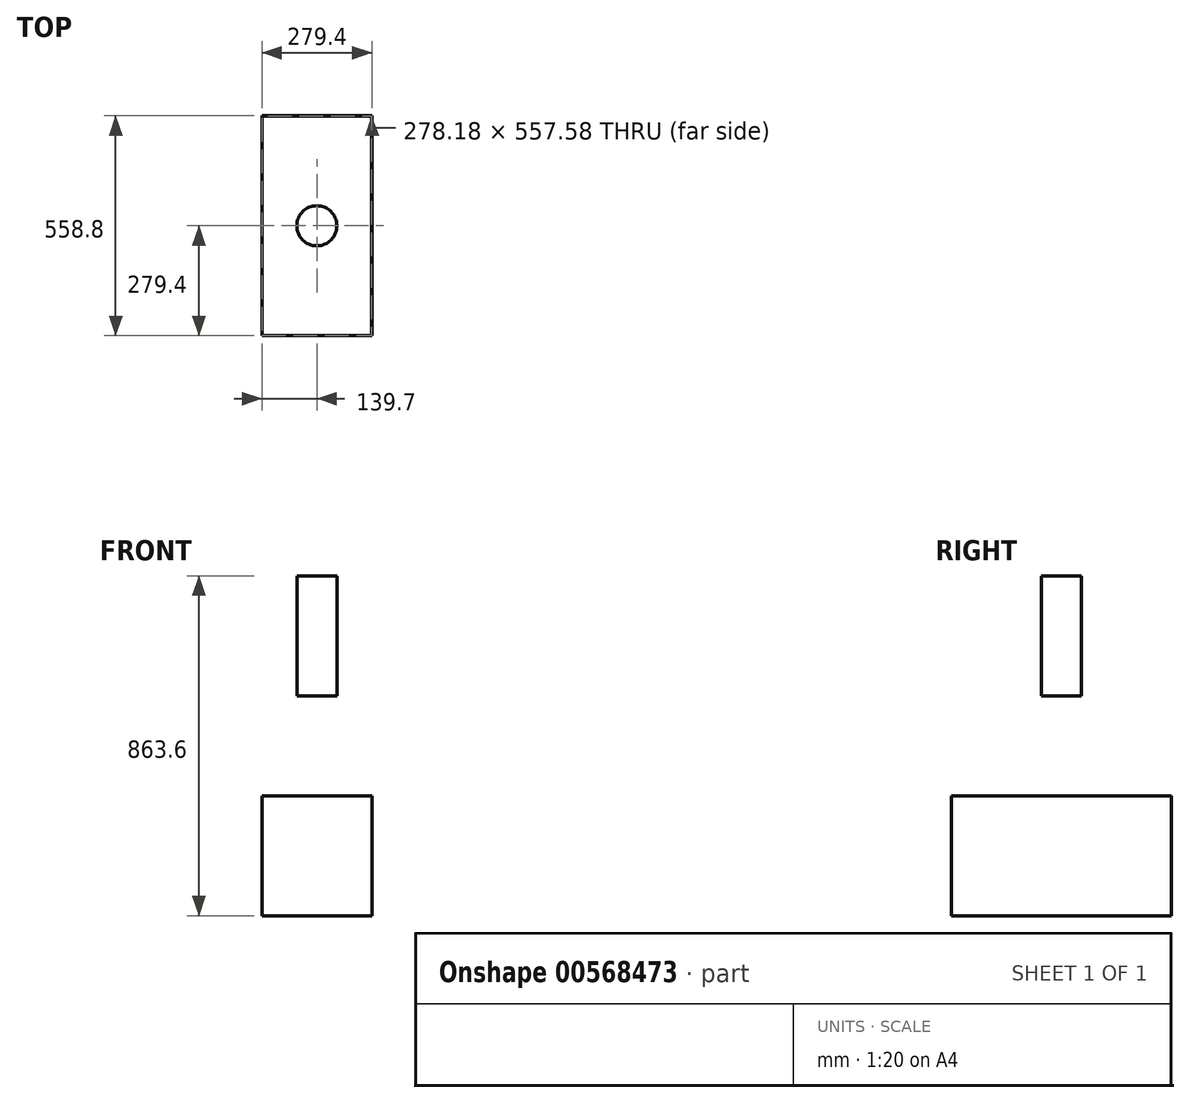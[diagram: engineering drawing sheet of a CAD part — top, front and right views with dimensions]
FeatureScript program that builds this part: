
annotation { "Feature Type Name" : "Feature", "Feature Type Description" : "" }
export const myFeature = defineFeature(function(context is Context, id is Id, definition is map)
    precondition{}
    {
        {
            var Q0;
            Q0=qCreatedBy(makeId("Top.planeOp"),FACE);
            var sketch = newSketch(context, id + "F0", { "sketchPlane" : qUnion([Q0])});
            skLineSegment(sketch, "E0.bottom", {"start": v(0, 0) * mm, "end": v(279.4, 0) * mm});
            skLineSegment(sketch, "E0.top", {"start": v(0, 558.8) * mm, "end": v(279.4, 558.8) * mm});
            skLineSegment(sketch, "E0.left", {"start": v(0, 0) * mm, "end": v(0, 558.8) * mm});
            skLineSegment(sketch, "E0.right", {"start": v(279.4, 0) * mm, "end": v(279.4, 558.8) * mm});
            skLineSegment(sketch, "E1.bottom", {"start": v(0.6, 0.6) * mm, "end": v(278.8, 0.6) * mm});
            skLineSegment(sketch, "E1.top", {"start": v(0.6, 558.2) * mm, "end": v(278.8, 558.2) * mm});
            skLineSegment(sketch, "E1.left", {"start": v(0.6, 0.6) * mm, "end": v(0.6, 558.2) * mm});
            skLineSegment(sketch, "E1.right", {"start": v(278.8, 0.6) * mm, "end": v(278.8, 558.2) * mm});
            skSolve(sketch);
        }
        {
            var Q0;
            Q0=makeQuery(id+"F0.imprint","IMPRINT",FACE,{"disambiguationData":[TD([[makeQuery(id+"F0.imprint","IMPRINT",EDGE,{"derivedFrom":sQuery(id+"F0.wireOp",EDGE,"E0.bottom")}),1.0]])]});
            extrude(context, id + "F1", {"entities" : qUnion([Q0]), "depth" : 304.8 * mm, "offsetDistance" : 25.4 * mm});
        }
        {
            var Q0;
            Q0=qCreatedBy(makeId("Top.planeOp"),FACE);
            cPlane(context, id + "F2", {"entities" : qUnion([Q0]), "cplaneType" : CPlaneType.OFFSET, "offset" : 304.8 * mm, "width" : 152.4 * mm, "height" : 152.4 * mm});
        }
        {
            var Q0;
            Q0=qCreatedBy(id+"F2.planeOp",FACE);
            var sketch = newSketch(context, id + "F3", { "sketchPlane" : qUnion([Q0])});
            skLineSegment(sketch, "E2.bottom", {"start": v(0, 558.8) * mm, "end": v(279.4, 558.8) * mm});
            skLineSegment(sketch, "E2.top", {"start": v(0, 0) * mm, "end": v(279.4, 0) * mm});
            skLineSegment(sketch, "E2.left", {"start": v(0, 558.8) * mm, "end": v(0, 0) * mm});
            skLineSegment(sketch, "E2.right", {"start": v(279.4, 558.8) * mm, "end": v(279.4, 0) * mm});
            skLineSegment(sketch, "E3.bottom", {"start": v(0.6, 558.2) * mm, "end": v(278.8, 558.2) * mm});
            skLineSegment(sketch, "E3.top", {"start": v(0.6, 0.6) * mm, "end": v(278.8, 0.6) * mm});
            skLineSegment(sketch, "E3.left", {"start": v(0.6, 558.2) * mm, "end": v(0.6, 0.6) * mm});
            skLineSegment(sketch, "E3.right", {"start": v(278.8, 558.2) * mm, "end": v(278.8, 0.6) * mm});
            skSolve(sketch);
        }
        {
            var Q0;
            Q0=qCreatedBy(id+"F2.planeOp",FACE);
            cPlane(context, id + "F4", {"entities" : qUnion([Q0]), "cplaneType" : CPlaneType.OFFSET, "offset" : 254 * mm, "width" : 152.4 * mm, "height" : 152.4 * mm});
        }
        {
            var Q0;
            Q0=qCreatedBy(id+"F4.planeOp",FACE);
            var sketch = newSketch(context, id + "F5", { "sketchPlane" : qUnion([Q0])});
            skLineSegment(sketch, "E4.bottom", {"start": v(0, 381) * mm, "end": v(279.4, 381) * mm});
            skLineSegment(sketch, "E4.top", {"start": v(0, 177.8) * mm, "end": v(279.4, 177.8) * mm});
            skLineSegment(sketch, "E4.left", {"start": v(0, 381) * mm, "end": v(0, 177.8) * mm});
            skLineSegment(sketch, "E4.right", {"start": v(279.4, 381) * mm, "end": v(279.4, 177.8) * mm});
            skSolve(sketch);
        }
        {
            var Q0;
            Q0=sQuery(id+"F3.wireOp",EDGE,"E2.right");
            var Q1;
            Q1=sQuery(id+"F5.wireOp",EDGE,"E4.right");
            loft(context, id + "F6", {"bodyType" : ToolBodyType.SURFACE, "wireProfilesArray" : [{ "wireProfileEntities" : qUnion([Q0]) }, { "wireProfileEntities" : qUnion([Q1]) }]});
        }
        {
            var Q0;
            Q0 = qSketchRegion(id + "F3", true);
            var Q1;
            Q1=makeQuery(id+"F1.opExtrude","CAP_EDGE",EDGE,{"disambiguationData":[OSD([sQuery(id+"F0.wireOp",EDGE,"E0.top")])],"isStart":false});
            var Q2;
            Q2=sQuery(id+"F5.wireOp",EDGE,"E4.bottom");
            loft(context, id + "F7", {"bodyType" : ToolBodyType.SURFACE, "sheetProfilesArray" : [{ "sheetProfileEntities" : qUnion([Q0]) }], "wireProfilesArray" : [{ "wireProfileEntities" : qUnion([Q1]) }, { "wireProfileEntities" : qUnion([Q2]) }]});
        }
        {
            var Q0;
            Q0=makeQuery(id+"F1.opExtrude","CAP_EDGE",EDGE,{"disambiguationData":[OSD([sQuery(id+"F0.wireOp",EDGE,"E0.left")])],"isStart":false});
            var Q1;
            Q1=sQuery(id+"F5.wireOp",EDGE,"E4.left");
            loft(context, id + "F8", {"bodyType" : ToolBodyType.SURFACE, "wireProfilesArray" : [{ "wireProfileEntities" : qUnion([Q0]) }, { "wireProfileEntities" : qUnion([Q1]) }]});
        }
        {
            var Q0;
            Q0=makeQuery(id+"F1.opExtrude","SWEPT_FACE",FACE,{"disambiguationData":[OSD([sQuery(id+"F0.wireOp",EDGE,"E0.bottom")])]});
            var Q1;
            Q1=makeQuery(id+"F1.opExtrude","CAP_EDGE",EDGE,{"disambiguationData":[OSD([sQuery(id+"F0.wireOp",EDGE,"E0.bottom")])],"isStart":false});
            var Q2;
            Q2=sQuery(id+"F5.wireOp",EDGE,"E4.top");
            loft(context, id + "F9", {"bodyType" : ToolBodyType.SURFACE, "sheetProfilesArray" : [{ "sheetProfileEntities" : qUnion([Q0]) }], "wireProfilesArray" : [{ "wireProfileEntities" : qUnion([Q1]) }, { "wireProfileEntities" : qUnion([Q2]) }]});
        }
        {
            var Q0;
            Q0=qCreatedBy(id+"F4.planeOp",FACE);
            var sketch = newSketch(context, id + "F10", { "sketchPlane" : qUnion([Q0])});
            skCircle(sketch, "E5", {"center": v(139.7, 279.4) * mm, "radius": 50.8 * mm});
            skSolve(sketch);
        }
        {
            var Q0;
            Q0 = qSketchRegion(id + "F10", true);
            extrude(context, id + "F11", {"entities" : qUnion([Q0]), "depth" : 304.8 * mm, "offsetDistance" : 25.4 * mm});
        }
        {
            var Q0;
            Q0=sQuery(id+"F5.wireOp",EDGE,"E4.right");
            var Q1;
            Q1=sQuery(id+"F5.wireOp",EDGE,"E4.left");
            loft(context, id + "F12", {"bodyType" : ToolBodyType.SURFACE, "wireProfilesArray" : [{ "wireProfileEntities" : qUnion([Q0]) }, { "wireProfileEntities" : qUnion([Q1]) }]});
        }
    });
